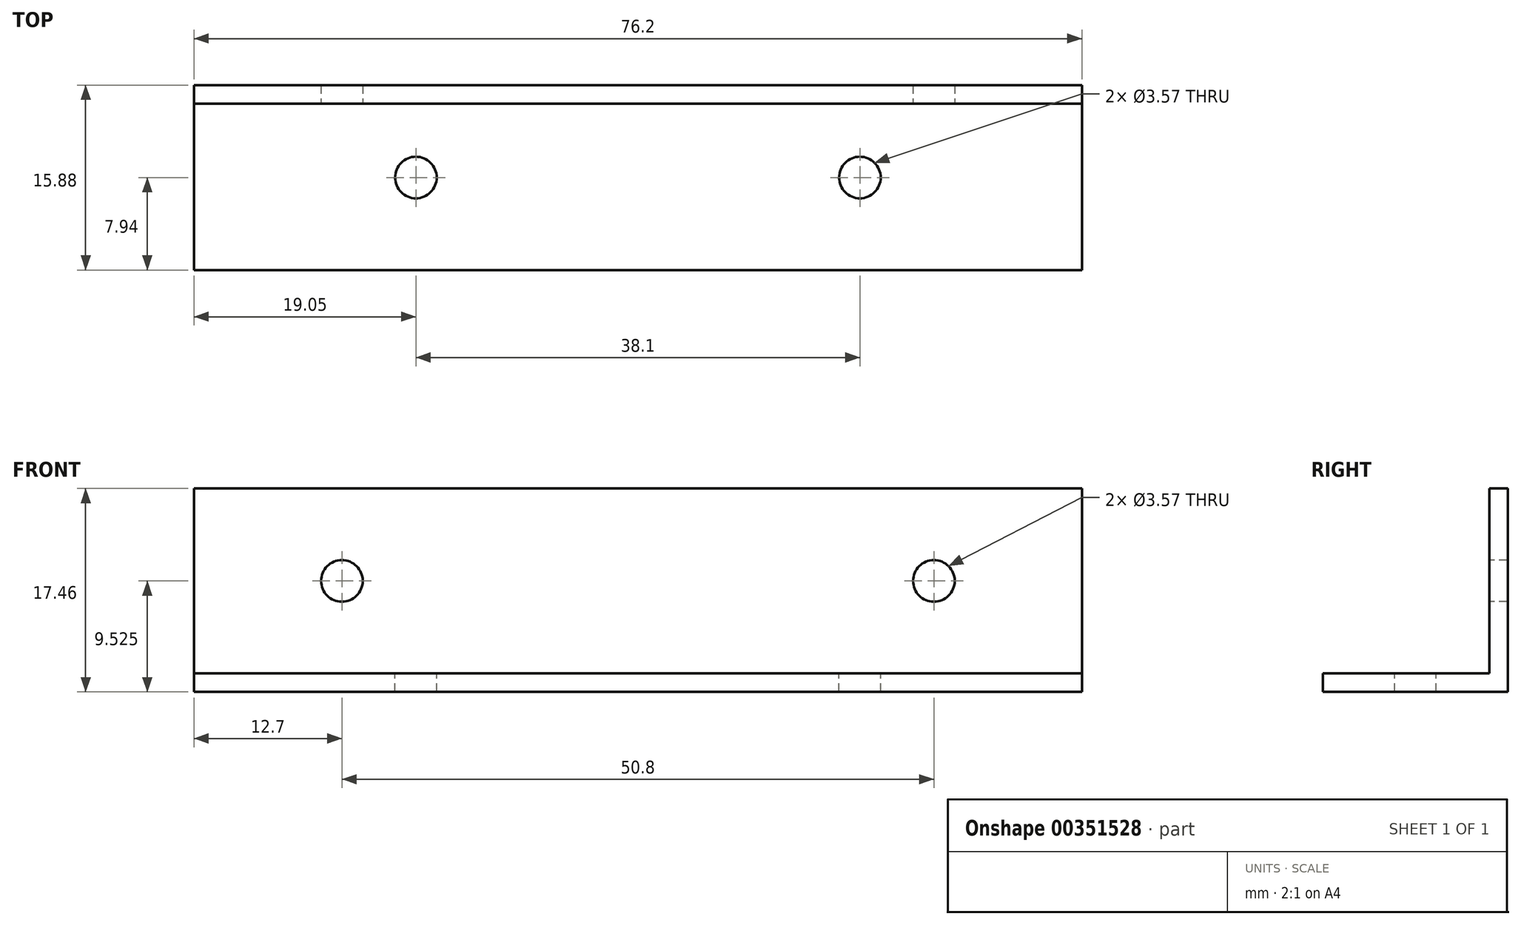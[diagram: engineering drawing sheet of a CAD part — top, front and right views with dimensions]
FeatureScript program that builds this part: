
annotation { "Feature Type Name" : "Feature", "Feature Type Description" : "" }
export const myFeature = defineFeature(function(context is Context, id is Id, definition is map)
    precondition{}
    {
        {
            var Q0;
            Q0=qCreatedBy(makeId("Top.planeOp"),FACE);
            var sketch = newSketch(context, id + "F0", { "sketchPlane" : qUnion([Q0])});
            skLineSegment(sketch, "E0.bottom", {"start": v(-38.1, 7.94) * mm, "end": v(38.1, 7.94) * mm});
            skLineSegment(sketch, "E0.top", {"start": v(-38.1, -7.94) * mm, "end": v(38.1, -7.94) * mm});
            skLineSegment(sketch, "E0.left", {"start": v(-38.1, 7.94) * mm, "end": v(-38.1, -7.94) * mm});
            skLineSegment(sketch, "E0.right", {"start": v(38.1, 7.94) * mm, "end": v(38.1, -7.94) * mm});
            skPoint(sketch, "E0.middle", {"position": v(0, 0) * mm});
            skSolve(sketch);
        }
        {
            var Q0;
            Q0 = qSketchRegion(id + "F0", true);
            extrude(context, id + "F1", {"entities" : qUnion([Q0]), "depth" : 1.59 * mm});
        }
        {
            var Q0;
            Q0=makeQuery(id+"F1.opExtrude","CAP_FACE",FACE,{"disambiguationData":[OSD([sQuery(id+"F0.wireOp",EDGE,"E0.bottom"),sQuery(id+"F0.wireOp",EDGE,"E0.top"),sQuery(id+"F0.wireOp",EDGE,"E0.left"),sQuery(id+"F0.wireOp",EDGE,"E0.right")])],"isStart":false});
            var sketch = newSketch(context, id + "F2", { "sketchPlane" : qUnion([Q0])});
            skLineSegment(sketch, "E1.bottom", {"start": v(-38.1, 7.94) * mm, "end": v(38.1, 7.94) * mm});
            skLineSegment(sketch, "E1.top", {"start": v(-38.1, 6.35) * mm, "end": v(38.1, 6.35) * mm});
            skLineSegment(sketch, "E1.left", {"start": v(-38.1, 7.94) * mm, "end": v(-38.1, 6.35) * mm});
            skLineSegment(sketch, "E1.right", {"start": v(38.1, 7.94) * mm, "end": v(38.1, 6.35) * mm});
            skSolve(sketch);
        }
        {
            var Q0;
            Q0 = qSketchRegion(id + "F2", true);
            extrude(context, id + "F3", {"entities" : qUnion([Q0]), "operationType" : NewBodyOperationType.ADD, "depth" : 15.88 * mm});
        }
        {
            var Q0;
            Q0=makeQuery(id+"F1.opExtrude","CAP_FACE",FACE,{"disambiguationData":[OSD([sQuery(id+"F0.wireOp",EDGE,"E0.bottom"),sQuery(id+"F0.wireOp",EDGE,"E0.top"),sQuery(id+"F0.wireOp",EDGE,"E0.left"),sQuery(id+"F0.wireOp",EDGE,"E0.right")])],"isStart":false});
            var sketch = newSketch(context, id + "F4", { "sketchPlane" : qUnion([Q0])});
            skCircle(sketch, "E2", {"center": v(-19.05, 0) * mm, "radius": 1.79 * mm});
            skCircle(sketch, "E3", {"center": v(19.05, 0) * mm, "radius": 1.79 * mm});
            skSolve(sketch);
        }
        {
            var Q0;
            Q0 = qSketchRegion(id + "F4", true);
            var Q1;
            Q1=makeQuery(id+"F1.opExtrude","CAP_FACE",FACE,{"disambiguationData":[OSD([sQuery(id+"F0.wireOp",EDGE,"E0.bottom"),sQuery(id+"F0.wireOp",EDGE,"E0.top"),sQuery(id+"F0.wireOp",EDGE,"E0.left"),sQuery(id+"F0.wireOp",EDGE,"E0.right")])],"isStart":true});
            extrude(context, id + "F5", {"entities" : qUnion([Q0]), "operationType" : NewBodyOperationType.REMOVE, "endBound" : BoundingType.UP_TO_SURFACE, "oppositeDirection" : true, "endBoundEntityFace" : qUnion([Q1]), "depth" : 25.4 * mm});
        }
        {
            var Q0;
            Q0=makeQuery(id+"F3.opExtrude","SWEPT_FACE",FACE,{"disambiguationData":[OSD([sQuery(id+"F2.wireOp",EDGE,"E1.top")])]});
            var sketch = newSketch(context, id + "F6", { "sketchPlane" : qUnion([Q0])});
            skCircle(sketch, "E4", {"center": v(-25.4, 9.52) * mm, "radius": 1.79 * mm});
            skCircle(sketch, "E5", {"center": v(25.4, 9.52) * mm, "radius": 1.79 * mm});
            skSolve(sketch);
        }
        {
            var Q0;
            Q0 = qSketchRegion(id + "F6", true);
            var Q1;
            Q1=makeQuery(id+"F3.boolean.opBoolean","MERGE",FACE,{"derivedFrom":[makeQuery(id+"F1.opExtrude","SWEPT_FACE",FACE,{"disambiguationData":[OSD([sQuery(id+"F0.wireOp",EDGE,"E0.bottom")])]}),makeQuery(id+"F3.opExtrude","SWEPT_FACE",FACE,{"disambiguationData":[OSD([sQuery(id+"F2.wireOp",EDGE,"E1.bottom")])]})]});
            extrude(context, id + "F7", {"entities" : qUnion([Q0]), "operationType" : NewBodyOperationType.REMOVE, "endBound" : BoundingType.UP_TO_SURFACE, "oppositeDirection" : true, "endBoundEntityFace" : qUnion([Q1]), "depth" : 25.4 * mm});
        }
    });
